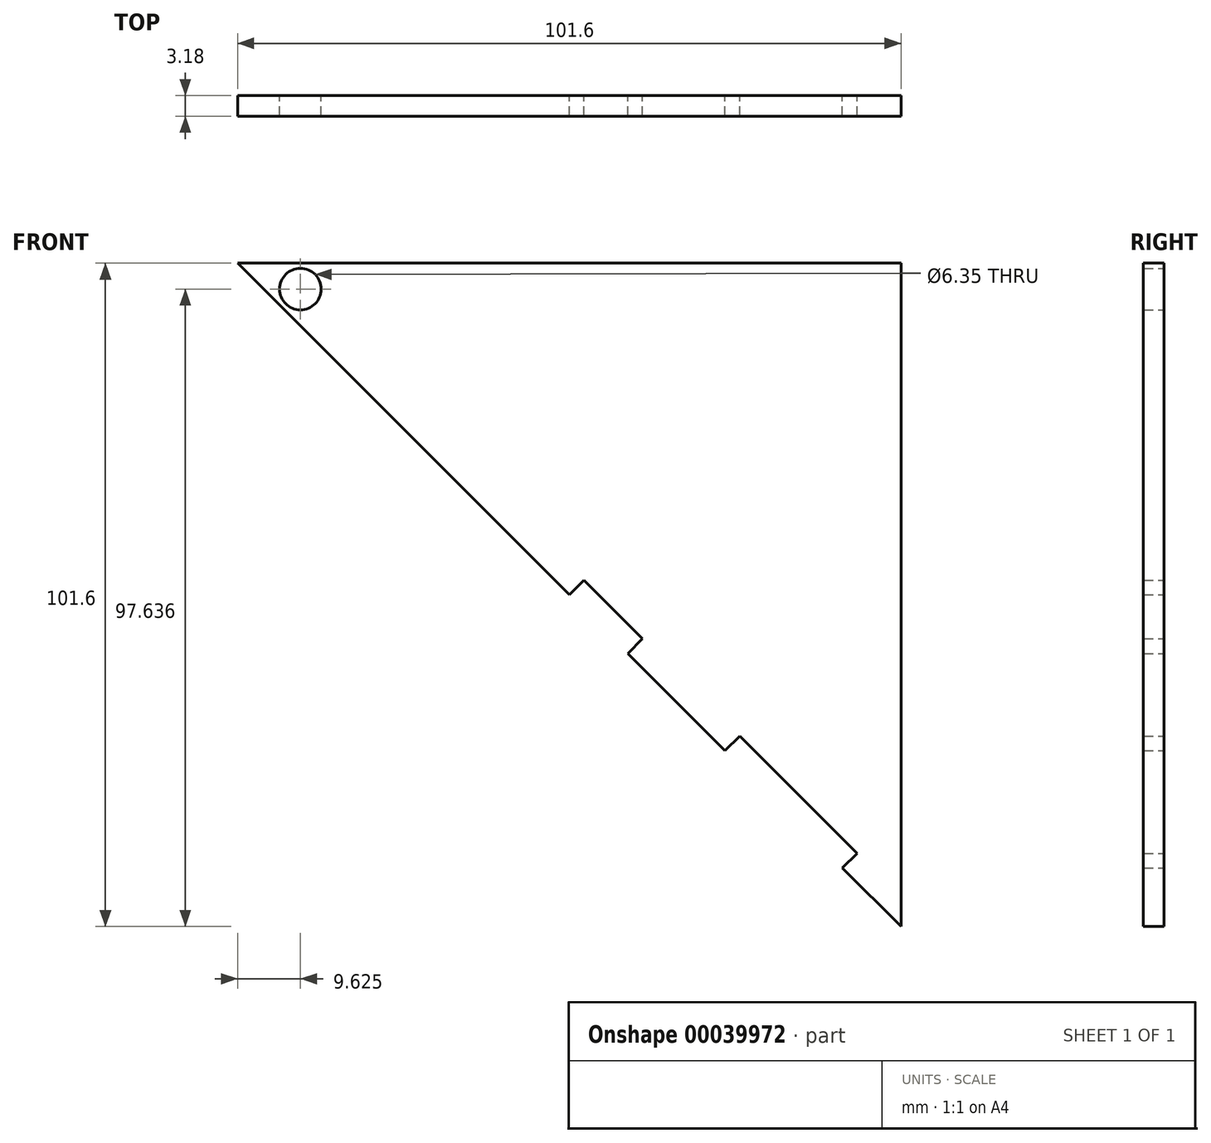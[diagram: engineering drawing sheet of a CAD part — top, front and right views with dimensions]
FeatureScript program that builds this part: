
annotation { "Feature Type Name" : "Feature", "Feature Type Description" : "" }
export const myFeature = defineFeature(function(context is Context, id is Id, definition is map)
    precondition{}
    {
        {
            var Q0;
            Q0=qCreatedBy(makeId("Front.planeOp"),FACE);
            var sketch = newSketch(context, id + "F0", { "sketchPlane" : qUnion([Q0])});
            skLineSegment(sketch, "E0", {"start": v(-62.93, 0) * mm, "end": v(38.67, 0) * mm});
            skLineSegment(sketch, "E1", {"start": v(38.67, 0) * mm, "end": v(38.67, -101.6) * mm});
            skLineSegment(sketch, "E2", {"start": v(-62.93, 0) * mm, "end": v(38.67, -101.6) * mm});
            skLineSegment(sketch, "E3", {"start": v(29.69, -92.62) * mm, "end": v(31.93, -90.37) * mm});
            skLineSegment(sketch, "E4", {"start": v(31.93, -90.37) * mm, "end": v(13.97, -72.41) * mm});
            skLineSegment(sketch, "E5", {"start": v(13.97, -72.41) * mm, "end": v(11.73, -74.66) * mm});
            skLineSegment(sketch, "E6", {"start": v(-3.15, -59.78) * mm, "end": v(-0.9, -57.54) * mm});
            skLineSegment(sketch, "E7", {"start": v(-0.9, -57.54) * mm, "end": v(-9.89, -48.55) * mm});
            skLineSegment(sketch, "E8", {"start": v(-9.89, -48.55) * mm, "end": v(-12.13, -50.8) * mm});
            skLineSegment(sketch, "E9", {"start": v(38.67, 0) * mm, "end": v(-49.71, -88.38) * mm, "construction": true});
            skCircle(sketch, "E10", {"center": v(-53.3, -3.96) * mm, "radius": 3.18 * mm});
            skSolve(sketch);
        }
        {
            var Q0;
            {var subQ4=sQuery(id+"F0.wireOp",EDGE,"E0");Q0=makeQuery(id+"F0.imprint","IMPRINT",FACE,{"disambiguationData":[TD([[makeQuery(id+"F0.imprint","IMPRINT",EDGE,{"derivedFrom":subQ4}),-1.0]])]});}
            extrude(context, id + "F1", {"entities" : qUnion([Q0]), "depth" : 3.17 * mm});
        }
    });
